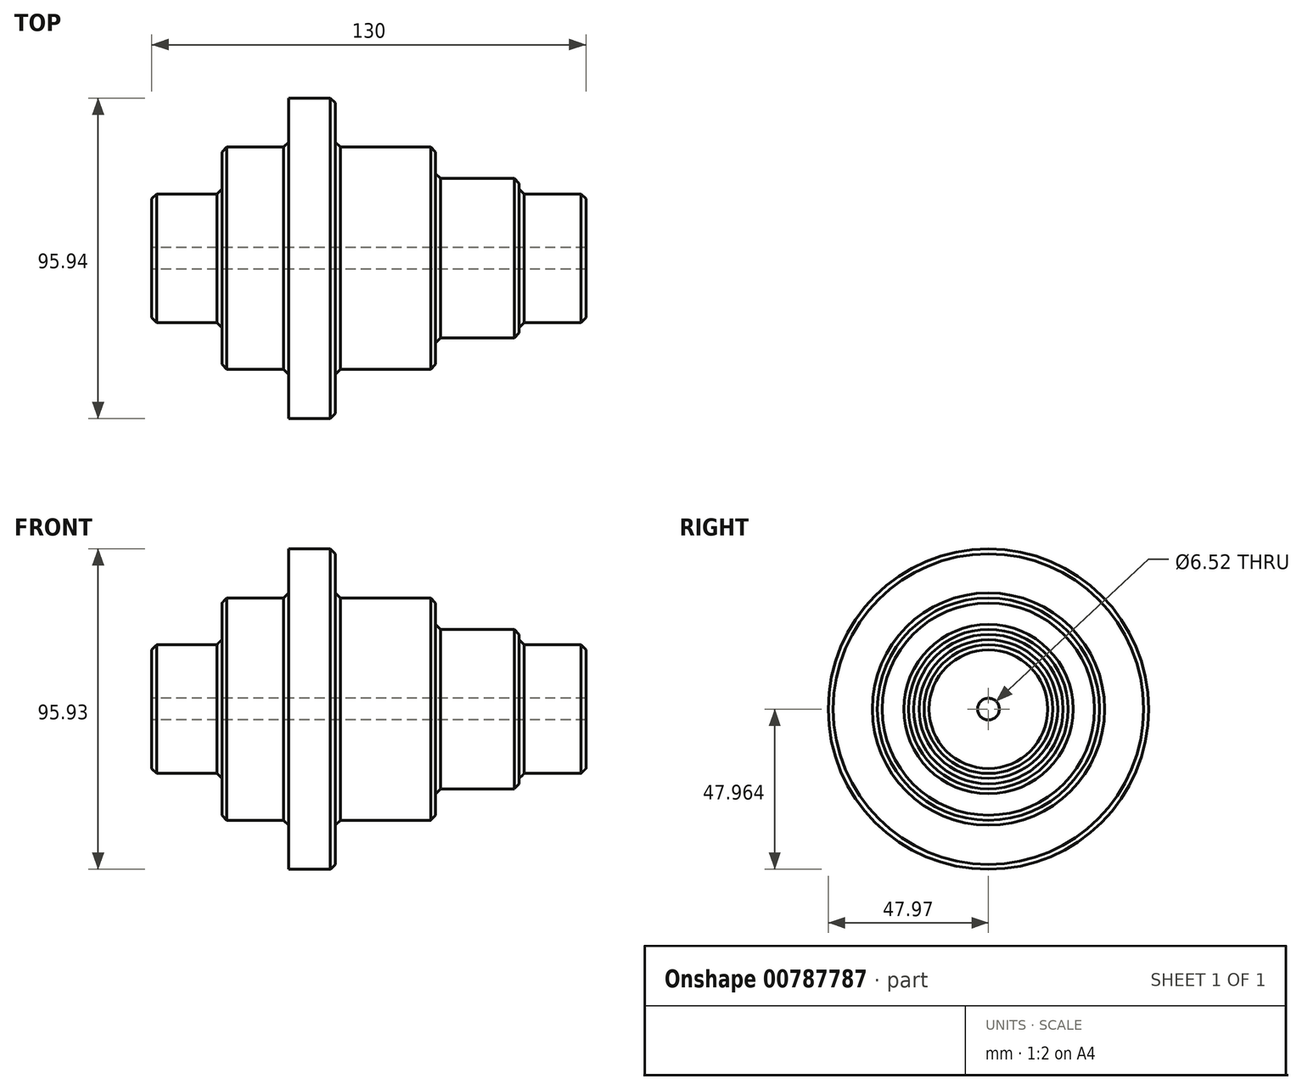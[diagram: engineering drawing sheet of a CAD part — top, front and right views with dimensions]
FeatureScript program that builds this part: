
annotation { "Feature Type Name" : "Feature", "Feature Type Description" : "" }
export const myFeature = defineFeature(function(context is Context, id is Id, definition is map)
    precondition{}
    {
        {
            var Q0;
            Q0=qCreatedBy(makeId("Front.planeOp"),FACE);
            var sketch = newSketch(context, id + "F0", { "sketchPlane" : qUnion([Q0])});
            skLineSegment(sketch, "E0", {"start": v(-95.26, -19.47) * mm, "end": v(34.74, -19.47) * mm});
            skLineSegment(sketch, "E1", {"start": v(-95.26, -19.47) * mm, "end": v(-95.26, -3.47) * mm});
            skLineSegment(sketch, "E2", {"start": v(-95.26, -3.47) * mm, "end": v(-74.26, -3.47) * mm});
            skLineSegment(sketch, "E3", {"start": v(-74.26, -3.47) * mm, "end": v(-74.26, 10.53) * mm});
            skLineSegment(sketch, "E4", {"start": v(-74.26, 10.53) * mm, "end": v(-54.26, 10.53) * mm});
            skLineSegment(sketch, "E5", {"start": v(-54.26, 10.53) * mm, "end": v(-54.26, 25.23) * mm});
            skLineSegment(sketch, "E6", {"start": v(-54.26, 25.23) * mm, "end": v(-40.26, 25.23) * mm});
            skLineSegment(sketch, "E7", {"start": v(-40.26, 25.23) * mm, "end": v(-40.26, 10.53) * mm});
            skLineSegment(sketch, "E8", {"start": v(-40.26, 10.53) * mm, "end": v(-10.26, 10.53) * mm});
            skLineSegment(sketch, "E9", {"start": v(-10.26, 10.53) * mm, "end": v(-10.26, 1.11) * mm});
            skLineSegment(sketch, "E10", {"start": v(-10.26, 1.11) * mm, "end": v(14.74, 1.11) * mm});
            skLineSegment(sketch, "E11", {"start": v(14.74, 1.11) * mm, "end": v(14.74, -3.47) * mm});
            skLineSegment(sketch, "E12", {"start": v(14.74, -3.47) * mm, "end": v(34.74, -3.47) * mm});
            skLineSegment(sketch, "E13", {"start": v(34.74, -3.47) * mm, "end": v(34.74, -19.47) * mm});
            skLineSegment(sketch, "E14", {"start": v(-95.26, -22.74) * mm, "end": v(34.67, -22.74) * mm, "construction": true});
            skSolve(sketch);
        }
        {
            var Q0;
            Q0=makeQuery(id+"F0.imprint","IMPRINT",FACE,{"disambiguationData":[TD([[makeQuery(id+"F0.imprint","IMPRINT",EDGE,{"derivedFrom":sQuery(id+"F0.wireOp",EDGE,"E0")}),1.0]])]});
            var Q1;
            Q1=sQuery(id+"F0.wireOp",EDGE,"E14");
            revolve(context, id + "F1", {"surfaceOperationType" : NewSurfaceOperationType.NEW, "entities" : qUnion([Q0]), "axis" : qUnion([Q1]), "revolveType" : RevolveType.FULL});
        }
        {
            var Q0;
            Q0=makeQuery(id+"F1.opRevolve","SWEPT_EDGE",EDGE,{"disambiguationData":[OSD([sQuery(id+"F0.wireOp",EDGE,"E1"),sQuery(id+"F0.wireOp",EDGE,"E2")])]});
            chamfer(context, id + "F2", {"entities" : qUnion([Q0]), "width" : 1.5 * mm, "tangentPropagation" : true});
        }
        {
            var Q0;
            Q0=makeQuery(id+"F1.opRevolve","SWEPT_EDGE",EDGE,{"disambiguationData":[OSD([sQuery(id+"F0.wireOp",EDGE,"E3"),sQuery(id+"F0.wireOp",EDGE,"E4")])]});
            chamfer(context, id + "F3", {"entities" : qUnion([Q0]), "width" : 1.5 * mm, "tangentPropagation" : true});
        }
        {
            var Q0;
            Q0=makeQuery(id+"F1.opRevolve","SWEPT_EDGE",EDGE,{"disambiguationData":[OSD([sQuery(id+"F0.wireOp",EDGE,"E6"),sQuery(id+"F0.wireOp",EDGE,"E7")])]});
            chamfer(context, id + "F4", {"entities" : qUnion([Q0]), "width" : 1.5 * mm, "tangentPropagation" : true});
        }
        {
            var Q0;
            Q0=makeQuery(id+"F1.opRevolve","SWEPT_EDGE",EDGE,{"disambiguationData":[OSD([sQuery(id+"F0.wireOp",EDGE,"E8"),sQuery(id+"F0.wireOp",EDGE,"E9")])]});
            chamfer(context, id + "F5", {"entities" : qUnion([Q0]), "width" : 1.5 * mm, "tangentPropagation" : true});
        }
        {
            var Q0;
            Q0=makeQuery(id+"F1.opRevolve","SWEPT_EDGE",EDGE,{"disambiguationData":[OSD([sQuery(id+"F0.wireOp",EDGE,"E10"),sQuery(id+"F0.wireOp",EDGE,"E11")])]});
            chamfer(context, id + "F6", {"entities" : qUnion([Q0]), "width" : 1.5 * mm, "tangentPropagation" : true});
        }
        {
            var Q0;
            Q0=makeQuery(id+"F1.opRevolve","SWEPT_EDGE",EDGE,{"disambiguationData":[OSD([sQuery(id+"F0.wireOp",EDGE,"E12"),sQuery(id+"F0.wireOp",EDGE,"E13")])]});
            chamfer(context, id + "F7", {"entities" : qUnion([Q0]), "width" : 1.5 * mm, "tangentPropagation" : true});
        }
        {
            var Q0;
            Q0=makeQuery(id+"F1.opRevolve","SWEPT_EDGE",EDGE,{"disambiguationData":[OSD([sQuery(id+"F0.wireOp",EDGE,"E4"),sQuery(id+"F0.wireOp",EDGE,"E5")])]});
            chamfer(context, id + "F8", {"entities" : qUnion([Q0]), "width" : 1.5 * mm, "tangentPropagation" : true});
        }
        {
            var Q0;
            Q0=makeQuery(id+"F1.opRevolve","SWEPT_EDGE",EDGE,{"disambiguationData":[OSD([sQuery(id+"F0.wireOp",EDGE,"E2"),sQuery(id+"F0.wireOp",EDGE,"E3")])]});
            chamfer(context, id + "F9", {"entities" : qUnion([Q0]), "width" : 1.5 * mm, "tangentPropagation" : true});
        }
        {
            var Q0;
            Q0=makeQuery(id+"F1.opRevolve","SWEPT_EDGE",EDGE,{"disambiguationData":[OSD([sQuery(id+"F0.wireOp",EDGE,"E7"),sQuery(id+"F0.wireOp",EDGE,"E8")])]});
            chamfer(context, id + "F10", {"entities" : qUnion([Q0]), "width" : 1.5 * mm, "tangentPropagation" : true});
        }
        {
            var Q0;
            Q0=makeQuery(id+"F1.opRevolve","SWEPT_EDGE",EDGE,{"disambiguationData":[OSD([sQuery(id+"F0.wireOp",EDGE,"E9"),sQuery(id+"F0.wireOp",EDGE,"E10")])]});
            chamfer(context, id + "F11", {"entities" : qUnion([Q0]), "width" : 1.5 * mm, "tangentPropagation" : true});
        }
        {
            var Q0;
            Q0=makeQuery(id+"F1.opRevolve","SWEPT_EDGE",EDGE,{"disambiguationData":[OSD([sQuery(id+"F0.wireOp",EDGE,"E11"),sQuery(id+"F0.wireOp",EDGE,"E12")])]});
            chamfer(context, id + "F12", {"entities" : qUnion([Q0]), "width" : 1.5 * mm, "tangentPropagation" : true});
        }
    });
